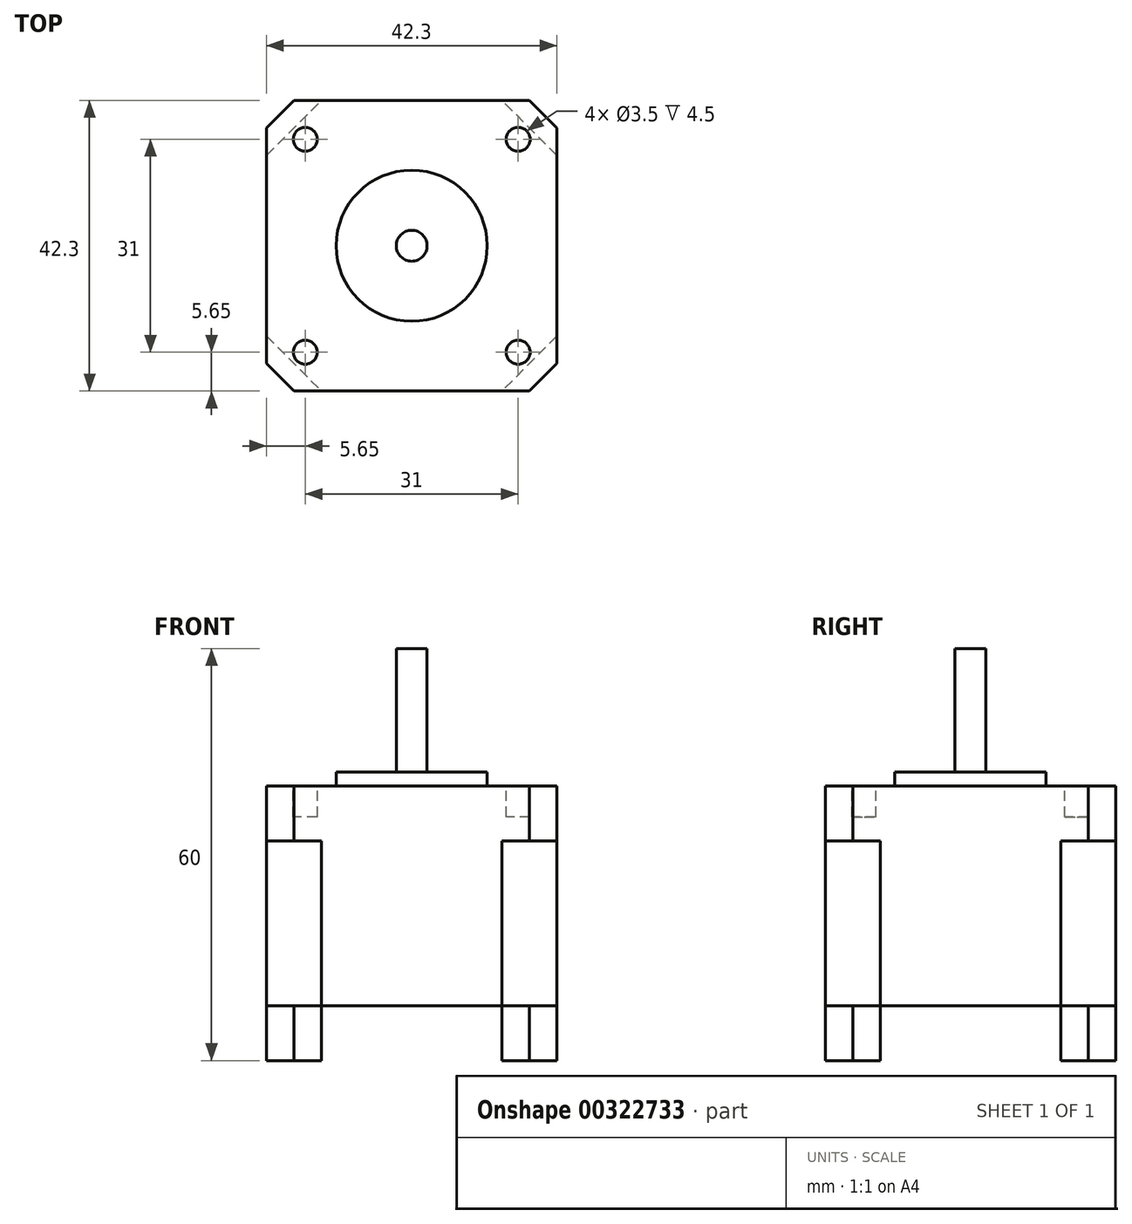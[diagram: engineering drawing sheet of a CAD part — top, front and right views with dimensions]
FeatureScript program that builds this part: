
annotation { "Feature Type Name" : "Feature", "Feature Type Description" : "" }
export const myFeature = defineFeature(function(context is Context, id is Id, definition is map)
    precondition{}
    {
        {
            assignVariable(context, id + "F0", {"name" : "motor", "anyValue" : 40});
        }
        {
            var Q0;
            Q0=qCreatedBy(makeId("Top.planeOp"),FACE);
            var sketch = newSketch(context, id + "F1", { "sketchPlane" : qUnion([Q0])});
            skLineSegment(sketch, "E0.bottom", {"start": v(17.15, 21.15) * mm, "end": v(-17.15, 21.15) * mm});
            skLineSegment(sketch, "E0.top", {"start": v(17.15, -21.15) * mm, "end": v(-17.15, -21.15) * mm});
            skLineSegment(sketch, "E0.left", {"start": v(21.15, 17.15) * mm, "end": v(21.15, -17.15) * mm});
            skLineSegment(sketch, "E0.right", {"start": v(-21.15, 17.15) * mm, "end": v(-21.15, -17.15) * mm});
            skPoint(sketch, "E0.middle", {"position": v(0, 0) * mm});
            skLineSegment(sketch, "E1", {"start": v(-17.15, 21.15) * mm, "end": v(-21.15, 17.15) * mm});
            skLineSegment(sketch, "E2.MirrorCS", {"start": v(17.15, 21.15) * mm, "end": v(21.15, 17.15) * mm});
            skLineSegment(sketch, "E3.MirrorCS", {"start": v(-17.15, -21.15) * mm, "end": v(-21.15, -17.15) * mm});
            skLineSegment(sketch, "E4.MirrorCS", {"start": v(17.15, -21.15) * mm, "end": v(21.15, -17.15) * mm});
            skPoint(sketch, "E5.orphan", {"position": v(-21.15, 21.15) * mm});
            skPoint(sketch, "E6.orphan", {"position": v(21.15, 21.15) * mm});
            skPoint(sketch, "E7.orphan", {"position": v(21.15, -21.15) * mm});
            skPoint(sketch, "E8.orphan", {"position": v(-21.15, -21.15) * mm});
            skCircle(sketch, "E9", {"center": v(-15.5, 15.5) * mm, "radius": 1.75 * mm});
            skCircle(sketch, "E10", {"center": v(0, 0) * mm, "radius": 11 * mm});
            skCircle(sketch, "E11.1.0", {"center": v(-15.5, -15.5) * mm, "radius": 1.75 * mm});
            skCircle(sketch, "E11.2.0", {"center": v(15.5, -15.5) * mm, "radius": 1.75 * mm});
            skCircle(sketch, "E12.1.3.0", {"center": v(15.5, 15.5) * mm, "radius": 1.75 * mm});
            skCircle(sketch, "E13", {"center": v(0, 0) * mm, "radius": 2.25 * mm});
            skSolve(sketch);
        }
        {
            var Q0;
            Q0=makeQuery(id+"F1.imprint","IMPRINT",FACE,{"disambiguationData":[TD([[makeQuery(id+"F1.imprint","IMPRINT",EDGE,{"derivedFrom":sQuery(id+"F1.wireOp",EDGE,"E10")}),1.0]])]});
            extrude(context, id + "F2", {"entities" : qUnion([Q0]), "depth" : 2 * mm});
        }
        {
            var Q0;
            Q0=makeQuery(id+"F1.imprint","IMPRINT",FACE,{"disambiguationData":[TD([[makeQuery(id+"F1.imprint","IMPRINT",EDGE,{"derivedFrom":sQuery(id+"F1.wireOp",EDGE,"E10")}),1.0]])]});
            var Q1;
            Q1=makeQuery(id+"F1.imprint","IMPRINT",FACE,{"disambiguationData":[TD([[makeQuery(id+"F1.imprint","IMPRINT",EDGE,{"derivedFrom":sQuery(id+"F1.wireOp",EDGE,"E0.bottom")}),1.0]])]});
            var Q2;
            Q2=makeQuery(id+"F1.imprint","IMPRINT",FACE,{"disambiguationData":[TD([[makeQuery(id+"F1.imprint","IMPRINT",EDGE,{"derivedFrom":sQuery(id+"F1.wireOp",EDGE,"E11.2.0")}),1.0]])]});
            var Q3;
            Q3=makeQuery(id+"F1.imprint","IMPRINT",FACE,{"disambiguationData":[TD([[makeQuery(id+"F1.imprint","IMPRINT",EDGE,{"derivedFrom":sQuery(id+"F1.wireOp",EDGE,"E11.1.0")}),1.0]])]});
            var Q4;
            Q4=makeQuery(id+"F1.imprint","IMPRINT",FACE,{"disambiguationData":[TD([[makeQuery(id+"F1.imprint","IMPRINT",EDGE,{"derivedFrom":sQuery(id+"F1.wireOp",EDGE,"E9")}),1.0]])]});
            var Q5;
            Q5=makeQuery(id+"F1.imprint","IMPRINT",FACE,{"disambiguationData":[TD([[makeQuery(id+"F1.imprint","IMPRINT",EDGE,{"derivedFrom":sQuery(id+"F1.wireOp",EDGE,"E12.1.3.0")}),1.0]])]});
            var Q6;
            Q6=makeQuery(id+"F1.imprint","IMPRINT",FACE,{"disambiguationData":[TD([[makeQuery(id+"F1.imprint","IMPRINT",EDGE,{"derivedFrom":sQuery(id+"F1.wireOp",EDGE,"E13")}),1.0]])]});
            extrude(context, id + "F3", {"entities" : qUnion([Q0, Q1, Q2, Q3, Q4, Q5, Q6]), "operationType" : NewBodyOperationType.ADD, "oppositeDirection" : true, "depth" : 8 * mm});
        }
        {
            var Q0;
            Q0=makeQuery(id+"F1.imprint","IMPRINT",FACE,{"disambiguationData":[TD([[makeQuery(id+"F1.imprint","IMPRINT",EDGE,{"derivedFrom":sQuery(id+"F1.wireOp",EDGE,"E9")}),1.0]])]});
            var Q1;
            Q1=makeQuery(id+"F1.imprint","IMPRINT",FACE,{"disambiguationData":[TD([[makeQuery(id+"F1.imprint","IMPRINT",EDGE,{"derivedFrom":sQuery(id+"F1.wireOp",EDGE,"E12.1.3.0")}),1.0]])]});
            var Q2;
            Q2=makeQuery(id+"F1.imprint","IMPRINT",FACE,{"disambiguationData":[TD([[makeQuery(id+"F1.imprint","IMPRINT",EDGE,{"derivedFrom":sQuery(id+"F1.wireOp",EDGE,"E11.2.0")}),1.0]])]});
            var Q3;
            Q3=makeQuery(id+"F1.imprint","IMPRINT",FACE,{"disambiguationData":[TD([[makeQuery(id+"F1.imprint","IMPRINT",EDGE,{"derivedFrom":sQuery(id+"F1.wireOp",EDGE,"E11.1.0")}),1.0]])]});
            extrude(context, id + "F4", {"entities" : qUnion([Q0, Q1, Q2, Q3]), "operationType" : NewBodyOperationType.REMOVE, "oppositeDirection" : true, "depth" : 4.5 * mm});
        }
        {
            var Q0;
            Q0=makeQuery(id+"F1.imprint","IMPRINT",FACE,{"disambiguationData":[TD([[makeQuery(id+"F1.imprint","IMPRINT",EDGE,{"derivedFrom":sQuery(id+"F1.wireOp",EDGE,"E13")}),1.0]])]});
            extrude(context, id + "F5", {"entities" : qUnion([Q0]), "operationType" : NewBodyOperationType.ADD, "depth" : 20 * mm});
        }
        {
            var Q0;
            Q0=makeQuery(id+"F3.opExtrude","CAP_FACE",FACE,{"disambiguationData":[OSD([sQuery(id+"F1.wireOp",EDGE,"E0.bottom"),sQuery(id+"F1.wireOp",EDGE,"E0.top"),sQuery(id+"F1.wireOp",EDGE,"E0.left"),sQuery(id+"F1.wireOp",EDGE,"E0.right"),sQuery(id+"F1.wireOp",EDGE,"E1"),sQuery(id+"F1.wireOp",EDGE,"E2.MirrorCS"),sQuery(id+"F1.wireOp",EDGE,"E3.MirrorCS"),sQuery(id+"F1.wireOp",EDGE,"E4.MirrorCS")])],"isStart":false});
            var sketch = newSketch(context, id + "F6", { "sketchPlane" : qUnion([Q0])});
            skLineSegment(sketch, "E14", {"start": v(-21.15, 13.15) * mm, "end": v(-13.15, 21.15) * mm});
            skLineSegment(sketch, "E15.MirrorCS", {"start": v(21.15, 13.15) * mm, "end": v(13.15, 21.15) * mm});
            skLineSegment(sketch, "E16.MirrorCS", {"start": v(-21.15, -13.15) * mm, "end": v(-13.15, -21.15) * mm});
            skLineSegment(sketch, "E17.MirrorCS", {"start": v(21.15, -13.15) * mm, "end": v(13.15, -21.15) * mm});
            skLineSegment(sketch, "E18", {"start": v(-13.15, 21.15) * mm, "end": v(13.15, 21.15) * mm});
            skLineSegment(sketch, "E19", {"start": v(21.15, 13.15) * mm, "end": v(21.15, -13.15) * mm});
            skLineSegment(sketch, "E20", {"start": v(13.15, -21.15) * mm, "end": v(-13.15, -21.15) * mm});
            skLineSegment(sketch, "E21", {"start": v(-21.15, -13.15) * mm, "end": v(-21.15, 13.15) * mm});
            skSolve(sketch);
        }
        {
            var Q0;
            Q0=makeQuery(id+"F6.imprint","IMPRINT",FACE,{"disambiguationData":[TD([[makeQuery(id+"F6.imprint","IMPRINT",EDGE,{"derivedFrom":sQuery(id+"F6.wireOp",EDGE,"E14")}),-1.0]])]});
            extrude(context, id + "F7", {"entities" : qUnion([Q0]), "operationType" : NewBodyOperationType.ADD, "depth" : (getVariable(context, 'motor') - 16) * mm});
        }
        {
            var Q0;
            Q0=makeQuery(id+"F7.opExtrude","CAP_FACE",FACE,{"disambiguationData":[OSD([sQuery(id+"F6.wireOp",EDGE,"E14"),sQuery(id+"F6.wireOp",EDGE,"E15.MirrorCS"),sQuery(id+"F6.wireOp",EDGE,"E16.MirrorCS"),sQuery(id+"F6.wireOp",EDGE,"E17.MirrorCS"),sQuery(id+"F6.wireOp",EDGE,"E18"),sQuery(id+"F6.wireOp",EDGE,"E19"),sQuery(id+"F6.wireOp",EDGE,"E20"),sQuery(id+"F6.wireOp",EDGE,"E21")])],"isStart":false});
            var sketch = newSketch(context, id + "F8", { "sketchPlane" : qUnion([Q0])});
            skLineSegment(sketch, "E22.bottom", {"start": v(-17.15, 21.15) * mm, "end": v(17.15, 21.15) * mm});
            skLineSegment(sketch, "E22.top", {"start": v(-17.15, -21.15) * mm, "end": v(17.15, -21.15) * mm});
            skLineSegment(sketch, "E22.left", {"start": v(-21.15, 17.15) * mm, "end": v(-21.15, -17.15) * mm});
            skLineSegment(sketch, "E22.right", {"start": v(21.15, 17.15) * mm, "end": v(21.15, -17.15) * mm});
            skPoint(sketch, "E22.middle", {"position": v(0, 0) * mm});
            skLineSegment(sketch, "E23", {"start": v(-21.15, 17.15) * mm, "end": v(-17.15, 21.15) * mm});
            skPoint(sketch, "E23.startSnap0", {"position": v(-17.15, 17.15) * mm});
            skLineSegment(sketch, "E24.MirrorCS", {"start": v(21.15, 17.15) * mm, "end": v(17.15, 21.15) * mm});
            skLineSegment(sketch, "E25.MirrorCS", {"start": v(-21.15, -17.15) * mm, "end": v(-17.15, -21.15) * mm});
            skLineSegment(sketch, "E26.MirrorCS", {"start": v(21.15, -17.15) * mm, "end": v(17.15, -21.15) * mm});
            skPoint(sketch, "E27.orphan", {"position": v(-21.15, 21.15) * mm});
            skPoint(sketch, "E28.orphan", {"position": v(21.15, 21.15) * mm});
            skPoint(sketch, "E29.orphan", {"position": v(21.15, -21.15) * mm});
            skPoint(sketch, "E30.orphan", {"position": v(-21.15, -21.15) * mm});
            skSolve(sketch);
        }
        {
            var Q0;
            {var subQ2=sQuery(id+"F8.wireOp",EDGE,"E23");Q0=makeQuery(id+"F8.imprint","IMPRINT",FACE,{"disambiguationData":[TD([[makeQuery(id+"F8.imprint","IMPRINT",EDGE,{"derivedFrom":subQ2}),-1.0]])]});}
            var Q1;
            {var subQ4=makeQuery(id+"F7.opExtrude","CAP_EDGE",EDGE,{"disambiguationData":[OSD([sQuery(id+"F6.wireOp",EDGE,"E14")])],"isStart":false});Q1=makeQuery(id+"F8.imprint","IMPRINT",FACE,{"disambiguationData":[TD([[makeQuery(id+"F8.imprint","IMPRINT",EDGE,{"derivedFrom":subQ4}),-1.0]])]});}
            var Q2;
            {var subQ2=sQuery(id+"F8.wireOp",EDGE,"E24.MirrorCS");Q2=makeQuery(id+"F8.imprint","IMPRINT",FACE,{"disambiguationData":[TD([[makeQuery(id+"F8.imprint","IMPRINT",EDGE,{"derivedFrom":subQ2}),1.0]])]});}
            var Q3;
            {var subQ2=sQuery(id+"F8.wireOp",EDGE,"E26.MirrorCS");Q3=makeQuery(id+"F8.imprint","IMPRINT",FACE,{"disambiguationData":[TD([[makeQuery(id+"F8.imprint","IMPRINT",EDGE,{"derivedFrom":subQ2}),-1.0]])]});}
            var Q4;
            {var subQ2=sQuery(id+"F8.wireOp",EDGE,"E25.MirrorCS");Q4=makeQuery(id+"F8.imprint","IMPRINT",FACE,{"disambiguationData":[TD([[makeQuery(id+"F8.imprint","IMPRINT",EDGE,{"derivedFrom":subQ2}),1.0]])]});}
            extrude(context, id + "F9", {"entities" : qUnion([Q0, Q1, Q2, Q3, Q4]), "operationType" : NewBodyOperationType.ADD, "depth" : 8 * mm});
        }
        {
            var Q0;
            Q0=makeQuery(id+"F9.opExtrude","CAP_FACE",FACE,{"disambiguationData":[OSD([sQuery(id+"F8.wireOp",EDGE,"E22.bottom"),sQuery(id+"F8.wireOp",EDGE,"E22.top"),sQuery(id+"F8.wireOp",EDGE,"E22.left"),sQuery(id+"F8.wireOp",EDGE,"E22.right"),sQuery(id+"F8.wireOp",EDGE,"E23"),sQuery(id+"F8.wireOp",EDGE,"E24.MirrorCS"),sQuery(id+"F8.wireOp",EDGE,"E25.MirrorCS"),sQuery(id+"F8.wireOp",EDGE,"E26.MirrorCS")])],"isStart":false});
            var sketch = newSketch(context, id + "F10", { "sketchPlane" : qUnion([Q0])});
            skCircle(sketch, "E31", {"center": v(0, 0) * mm, "radius": 4 * mm});
            skSolve(sketch);
        }
        {
            var Q0;
            Q0=makeQuery(id+"F10.imprint","IMPRINT",FACE,{"disambiguationData":[TD([[makeQuery(id+"F10.imprint","IMPRINT",EDGE,{"derivedFrom":sQuery(id+"F10.wireOp",EDGE,"E31")}),1.0]])]});
            extrude(context, id + "F11", {"entities" : qUnion([Q0]), "operationType" : NewBodyOperationType.REMOVE, "oppositeDirection" : true, "depth" : 1 * mm});
        }
    });
